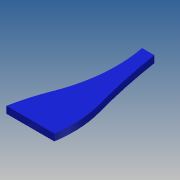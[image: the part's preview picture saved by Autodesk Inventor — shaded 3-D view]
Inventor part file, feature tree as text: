
AUTODESK INVENTOR PART (.ipt)
format: ipt  version: 2014 (Build 180170000, 170)  size: 127,488 bytes
history: native  units: mm
features: extrude x1
ambient origin geometry x8: Origin, YZ Plane, XZ Plane, XY Plane, X Axis, Y Axis, Z Axis, Center Point
bodies: Body1 (feature_tree)
feature tree (1):
  extrude  "Extrusion10"  Depth=1000.0mm
